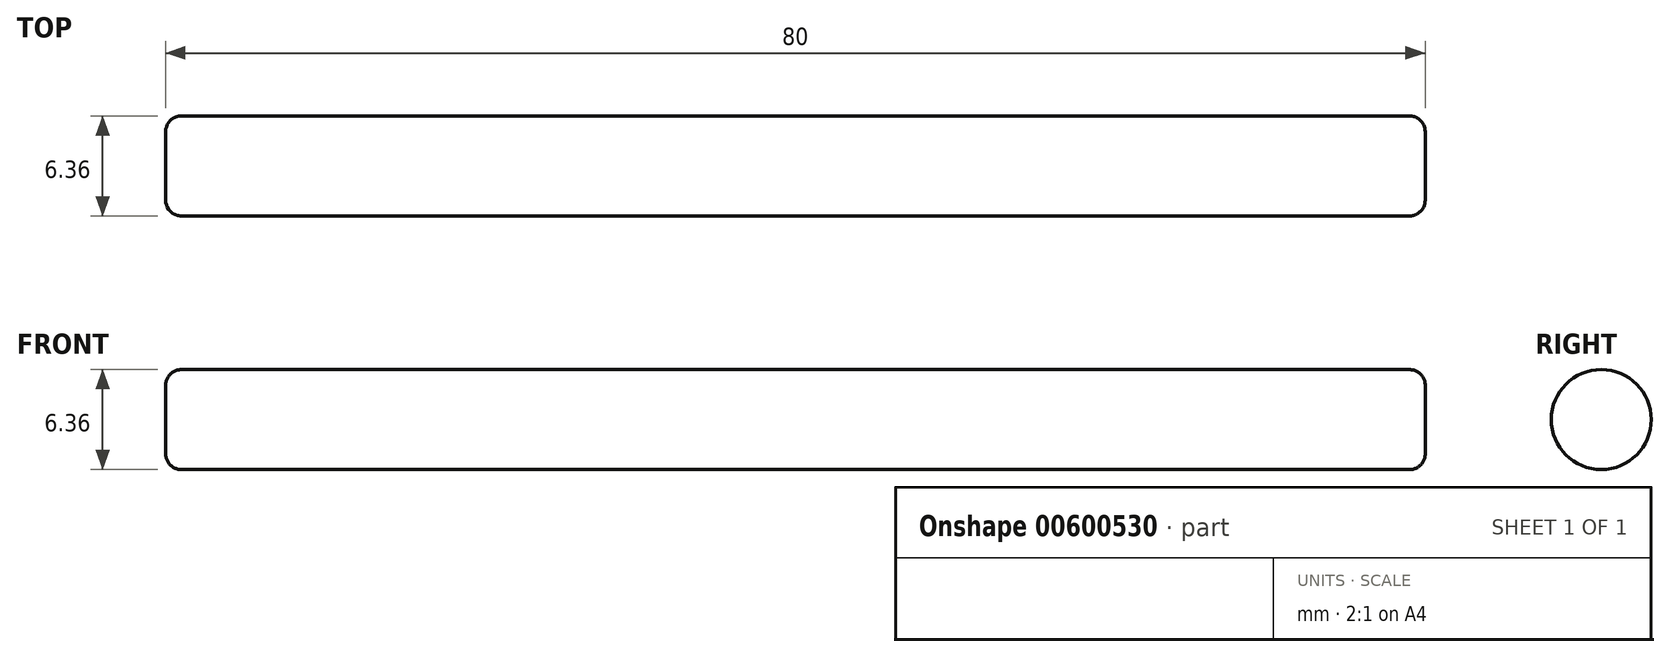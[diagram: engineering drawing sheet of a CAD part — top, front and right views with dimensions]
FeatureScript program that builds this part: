
annotation { "Feature Type Name" : "Feature", "Feature Type Description" : "" }
export const myFeature = defineFeature(function(context is Context, id is Id, definition is map)
    precondition{}
    {
        {
            var Q0;
            Q0=qCreatedBy(makeId("Right.planeOp"),FACE);
            var sketch = newSketch(context, id + "F0", { "sketchPlane" : qUnion([Q0])});
            skCircle(sketch, "E0", {"center": v(0, 0) * mm, "radius": 3.18 * mm});
            skSolve(sketch);
        }
        {
            var Q0;
            Q0 = qSketchRegion(id + "F0", true);
            extrude(context, id + "F1", {"entities" : qUnion([Q0]), "depth" : 80 * mm, "offsetDistance" : 25 * mm});
        }
        {
            var Q0;
            Q0=makeQuery(id+"F1.opExtrude","CAP_EDGE",EDGE,{"disambiguationData":[OSD([sQuery(id+"F0.wireOp",EDGE,"E0")])],"isStart":false});
            var Q1;
            Q1=makeQuery(id+"F1.opExtrude","CAP_EDGE",EDGE,{"disambiguationData":[OSD([sQuery(id+"F0.wireOp",EDGE,"E0")])],"isStart":true});
            fillet(context, id + "F2", {"entities" : qUnion([Q0, Q1]), "radius" : 1 * mm, "tangentPropagation" : true, "allowEdgeOverflow" : false});
        }
    });
